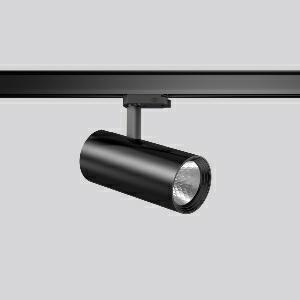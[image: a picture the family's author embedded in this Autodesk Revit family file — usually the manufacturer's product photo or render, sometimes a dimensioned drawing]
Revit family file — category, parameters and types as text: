
# Revit family: deecos_s_mini_742203_003_1_76_4003
name_source: partatom
category: Lighting Fixtures
units: mm (PartAtom-declared; Revit-internal decimal feet)

## family parameters
Cut with Voids When Loaded = No
Host = Face
Light Source = No
Part Type = Normal
Room Calculation Point = No
Round Connector Dimension = Use Diameter
Shared = No

## types (1)
- DEECOS S mini (1 x LED Modul 940, 3800 lm, 4000)
    Apparent Load = 29 VA
    Approval mark = CE
    CIE Flux Codes = 100 100 100 100 100
    Color Rendering = 92
    Color Temperature = 4000
    Default Elevation = 1800 mm
    Description = Series: DEECOS S mini
LED surface-mounted projector in modern design with no visible cooling ribs. Housing: die-cast aluminium, powder-coated. Rotation range: 356°. Swivel range: 90°. Black plastic ring and recessed LED to prevent glare from the side. Optical assembly with reflector made of MIRO-Silver with 98% total light reflection for outstanding efficiency - can be changed without tools. Best colour rendering index Ra>90. With adapter for RZB 3-circuit DALI tracks. Suitable for Track on ceiling, Wall track. High quality converter without flickering and stroboscopic effect. The following accessories can be mounted without use of tools: interchangeable lenses, decorative glasses, honeycomb louvre, clear and frosted diffusers, white interchangeable plastic ring. 
Colour: deep black, matt (RAL 9005)
Diameter: 87 mm
Height: 214 mm
Lamp: LED
Socket: without socket
Colour temperature: 4000K
Colour rendering index (CRI): 92
System power: 29 W
Rated luminous flux: 3800 lm
Luminous efficiency: 131 lm/W
Control gear: Converter, dimmable, DALI
Protection class: I
Type of protection: IP 20
    Height = 214 mm
    Lamp = 1 x LED Modul 940
    Lamp Light Flux = 3800 lm
    Lamp count = 1
    Length = 87 mm
    Lifetime = 50000 h
    Luminous efficacy = 131 lm/W
    Manufacturer = RZB
    ModVariant = No
    Model = 742203.003.1.76
    Mounting Place = Ceiling
    Mounting Type = Rail mounted
    Number of Poles = 1
    OnlyDefault = Yes
    Power Factor = 1
    Product Name = DEECOS S mini
    Product group = Track mounted projectors
    ProductGroupID = 301
    Protection Class = Protection class I
    Protection Degree = IP 20
    RLX_Detail_Level = 1
    RLX_Emergency_Light_Flux = 0 lm
    RLX_Emergency_Type = 0
    RLX_Emergency_Type_DB = No
    RlxData = <blob elided: 38641 chars, md5=b713a64d>
    Socket = socket
    Standby Power = 0 W
    System Light Flux = 3800 lm
    System Power = 29 W
    Type Comments = Product without accessories
    Type Image = 741926.003.jpg
    URL = http://relux.com
    VarID = ---
    Voltage = 230 V
    Voltage Range = 220-240 V
    Weight = 0.00 kg
    Width = 0 mm  [stored 0 ft]

note: [stored X ft] marks values corroborated as IEEE doubles in the binary element streams (Revit-internal decimal feet)

## geometry (parser evidence)
native form markers: Blend x4, Sweep x12
no freeform markers — native parametric forms only
